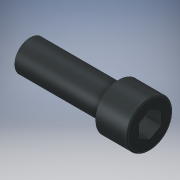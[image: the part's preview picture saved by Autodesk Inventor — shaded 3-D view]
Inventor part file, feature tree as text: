
AUTODESK INVENTOR PART (.ipt)
format: ipt  version: 2019 (Build 230136000, 136)  size: 125,952 bytes
history: native  units: mm
features: extrude x3, sketch x3, plane x1, fillet x1
ambient origin geometry x8: Origin, YZ Plane, XZ Plane, XY Plane, X Axis, Y Axis, Z Axis, Center Point
bodies: Solid1 (feature_tree)
feature tree (8):
  extrude  "Extrusion1"  Depth=10.0mm TaperAngle=0.0deg
  extrude  "Extrusion2"  Depth=3.5mm TaperAngle=0.0deg
  plane  "Work Plane1"
  extrude  "Extrusion3"  Depth=0.2mm
  fillet  "Fillet2"  Radius=1.75mm
  sketch  "Sketch1"  dims[d0=3.5mm d1=10.0mm d2=0.0mm]
  sketch  "Sketch2"  dims[d3=5.25mm d4=3.5mm d5=0.0mm]
  sketch  "Sketch3"  dims[d9=2.8mm d10=1.212436mm d11=1.75mm d12=0.0mm d13=0.2mm]
